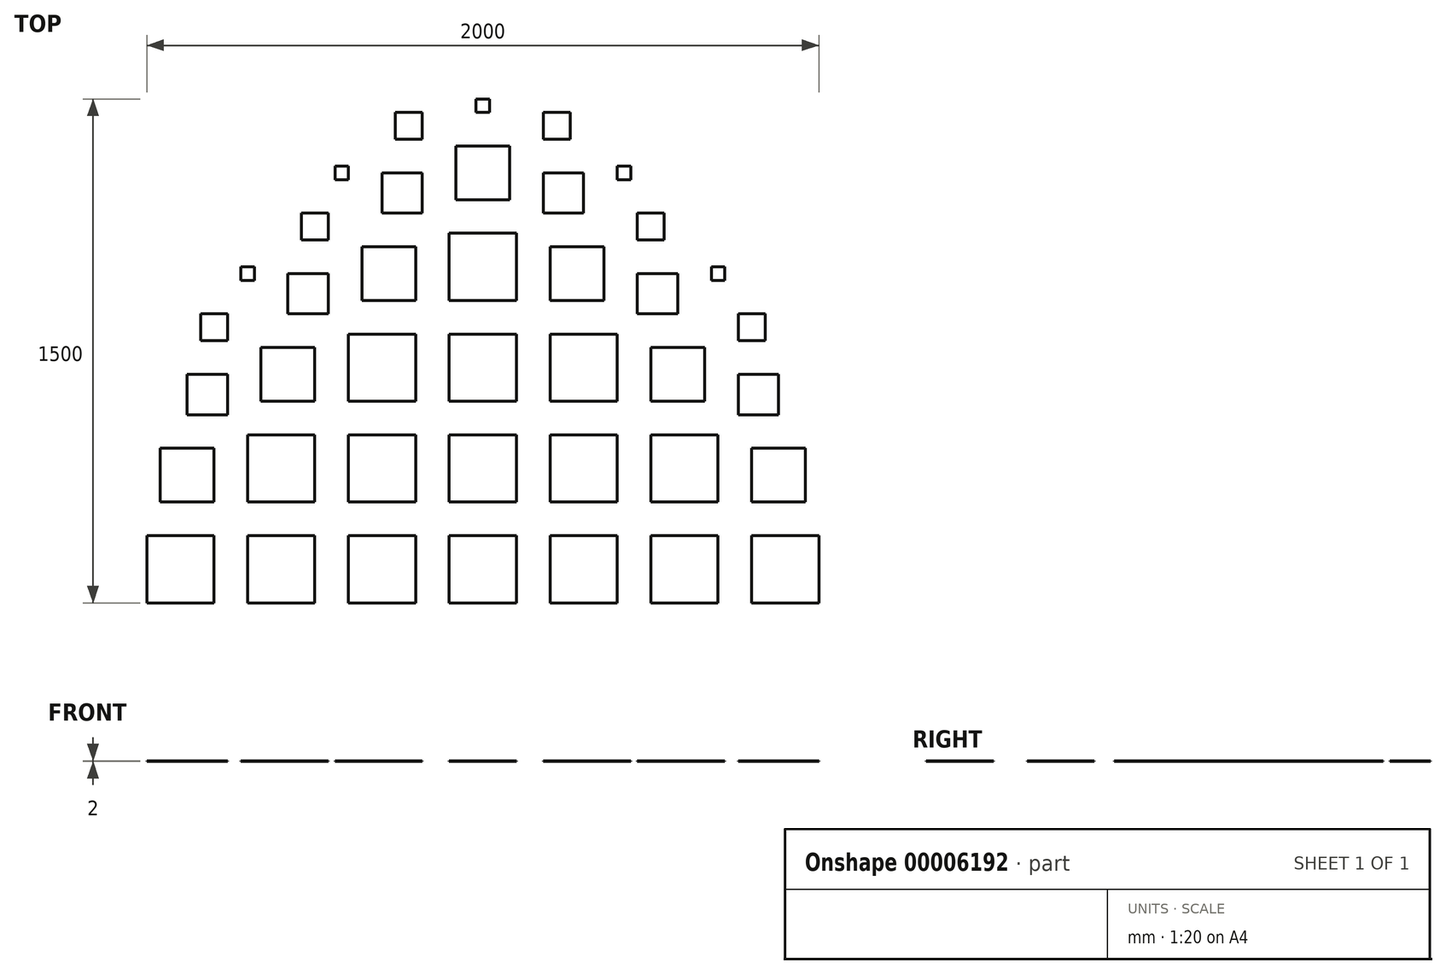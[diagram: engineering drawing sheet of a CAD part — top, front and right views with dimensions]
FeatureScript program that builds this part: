
annotation { "Feature Type Name" : "Feature", "Feature Type Description" : "" }
export const myFeature = defineFeature(function(context is Context, id is Id, definition is map)
    precondition{}
    {
        {
            var Q0;
            Q0=qCreatedBy(makeId("Top.planeOp"),FACE);
            var sketch = newSketch(context, id + "F0", { "sketchPlane" : qUnion([Q0])});
            skLineSegment(sketch, "E0.rect.bottom", {"start": v(100, 100) * mm, "end": v(-100, 100) * mm});
            skLineSegment(sketch, "E0.rect.top", {"start": v(100, -100) * mm, "end": v(-100, -100) * mm});
            skLineSegment(sketch, "E0.rect.left", {"start": v(100, 100) * mm, "end": v(100, -100) * mm});
            skLineSegment(sketch, "E0.rect.right", {"start": v(-100, 100) * mm, "end": v(-100, -100) * mm});
            skPoint(sketch, "E0.rect.middle", {"position": v(0, 0) * mm});
            skLineSegment(sketch, "E1.0.1.1", {"start": v(100, 200) * mm, "end": v(-60, 200) * mm});
            skLineSegment(sketch, "E1.0.1.3", {"start": v(100, 360) * mm, "end": v(100, 200) * mm});
            skLineSegment(sketch, "E1.1.0.0", {"start": v(200, 100) * mm, "end": v(200, -100) * mm});
            skLineSegment(sketch, "E1.1.0.1", {"start": v(400, -100) * mm, "end": v(200, -100) * mm});
            skLineSegment(sketch, "E1.1.0.2", {"start": v(400, 100) * mm, "end": v(200, 100) * mm});
            skLineSegment(sketch, "E1.1.0.3", {"start": v(400, 100) * mm, "end": v(400, -100) * mm});
            skLineSegment(sketch, "E1.1.1.0", {"start": v(200, 400) * mm, "end": v(200, 200) * mm});
            skLineSegment(sketch, "E1.1.1.1", {"start": v(400, 200) * mm, "end": v(200, 200) * mm});
            skLineSegment(sketch, "E1.1.1.2", {"start": v(400, 400) * mm, "end": v(200, 400) * mm});
            skLineSegment(sketch, "E1.1.1.3", {"start": v(400, 400) * mm, "end": v(400, 200) * mm});
            skLineSegment(sketch, "E1.2.0.0", {"start": v(500, 100) * mm, "end": v(500, -100) * mm});
            skLineSegment(sketch, "E1.2.0.1", {"start": v(700, -100) * mm, "end": v(500, -100) * mm});
            skLineSegment(sketch, "E1.2.0.2", {"start": v(700, 100) * mm, "end": v(500, 100) * mm});
            skLineSegment(sketch, "E1.2.0.3", {"start": v(700, 100) * mm, "end": v(700, -100) * mm});
            skLineSegment(sketch, "E1.2.1.0", {"start": v(500, 400) * mm, "end": v(500, 200) * mm});
            skLineSegment(sketch, "E1.2.1.1", {"start": v(700, 200) * mm, "end": v(500, 200) * mm});
            skLineSegment(sketch, "E1.2.1.2", {"start": v(700, 400) * mm, "end": v(500, 400) * mm});
            skLineSegment(sketch, "E1.2.1.3", {"start": v(700, 400) * mm, "end": v(700, 200) * mm});
            skLineSegment(sketch, "E1.3.0.0", {"start": v(800, 100) * mm, "end": v(800, -100) * mm});
            skLineSegment(sketch, "E1.3.0.1", {"start": v(1000, -100) * mm, "end": v(800, -100) * mm});
            skLineSegment(sketch, "E1.3.0.2", {"start": v(1000, 100) * mm, "end": v(800, 100) * mm});
            skLineSegment(sketch, "E1.3.0.3", {"start": v(1000, 100) * mm, "end": v(1000, -100) * mm});
            skLineSegment(sketch, "E1.3.1.0", {"start": v(800, 400) * mm, "end": v(800, 200) * mm});
            skLineSegment(sketch, "E1.3.1.1", {"start": v(1000, 200) * mm, "end": v(800, 200) * mm});
            skLineSegment(sketch, "E1.3.1.2", {"start": v(1000, 400) * mm, "end": v(800, 400) * mm});
            skLineSegment(sketch, "E1.3.1.3", {"start": v(1000, 400) * mm, "end": v(1000, 200) * mm});
            skLineSegment(sketch, "E1.4.0.0", {"start": v(1100, 100) * mm, "end": v(1100, -100) * mm});
            skLineSegment(sketch, "E1.4.0.1", {"start": v(1300, -100) * mm, "end": v(1100, -100) * mm});
            skLineSegment(sketch, "E1.4.0.2", {"start": v(1300, 100) * mm, "end": v(1100, 100) * mm});
            skLineSegment(sketch, "E1.4.0.3", {"start": v(1300, 100) * mm, "end": v(1300, -100) * mm});
            skLineSegment(sketch, "E1.4.1.0", {"start": v(1100, 400) * mm, "end": v(1100, 200) * mm});
            skLineSegment(sketch, "E1.4.1.1", {"start": v(1300, 200) * mm, "end": v(1100, 200) * mm});
            skLineSegment(sketch, "E1.4.1.2", {"start": v(1300, 400) * mm, "end": v(1100, 400) * mm});
            skLineSegment(sketch, "E1.4.1.3", {"start": v(1300, 400) * mm, "end": v(1300, 200) * mm});
            skLineSegment(sketch, "E1.5.0.0", {"start": v(1400, 100) * mm, "end": v(1400, -100) * mm});
            skLineSegment(sketch, "E1.5.0.1", {"start": v(1600, -100) * mm, "end": v(1400, -100) * mm});
            skLineSegment(sketch, "E1.5.0.2", {"start": v(1600, 100) * mm, "end": v(1400, 100) * mm});
            skLineSegment(sketch, "E1.5.0.3", {"start": v(1600, 100) * mm, "end": v(1600, -100) * mm});
            skLineSegment(sketch, "E1.5.1.0", {"start": v(1400, 400) * mm, "end": v(1400, 200) * mm});
            skLineSegment(sketch, "E1.5.1.1", {"start": v(1600, 200) * mm, "end": v(1400, 200) * mm});
            skLineSegment(sketch, "E1.5.1.2", {"start": v(1600, 400) * mm, "end": v(1400, 400) * mm});
            skLineSegment(sketch, "E1.5.1.3", {"start": v(1600, 400) * mm, "end": v(1600, 200) * mm});
            skLineSegment(sketch, "E1.6.0.0", {"start": v(1700, 100) * mm, "end": v(1700, -100) * mm});
            skLineSegment(sketch, "E1.6.0.1", {"start": v(1900, -100) * mm, "end": v(1700, -100) * mm});
            skLineSegment(sketch, "E1.6.0.2", {"start": v(1900, 100) * mm, "end": v(1700, 100) * mm});
            skLineSegment(sketch, "E1.6.0.3", {"start": v(1900, 100) * mm, "end": v(1900, -100) * mm});
            skLineSegment(sketch, "E1.6.1.0", {"start": v(1700, 360) * mm, "end": v(1700, 200) * mm});
            skLineSegment(sketch, "E1.6.1.1", {"start": v(1860, 200) * mm, "end": v(1700, 200) * mm});
            skLineSegment(sketch, "E1.direction1", {"start": v(-100, 100) * mm, "end": v(200, 100) * mm, "construction": true});
            skLineSegment(sketch, "E1.direction2", {"start": v(-100, 100) * mm, "end": v(-100, 200) * mm, "construction": true});
            skLineSegment(sketch, "E2", {"start": v(-60, 200) * mm, "end": v(-60, 360) * mm});
            skLineSegment(sketch, "E3", {"start": v(-60, 360) * mm, "end": v(100, 360) * mm});
            skPoint(sketch, "E4.orphan", {"position": v(100, 400) * mm});
            skLineSegment(sketch, "E5", {"start": v(1860, 200) * mm, "end": v(1860, 360) * mm});
            skLineSegment(sketch, "E6", {"start": v(1860, 360) * mm, "end": v(1700, 360) * mm});
            skPoint(sketch, "E7.orphan", {"position": v(1700, 400) * mm});
            skPoint(sketch, "E8.orphan", {"position": v(1900, 200) * mm});
            skLineSegment(sketch, "E9.0.1.0", {"start": v(700, 700) * mm, "end": v(500, 700) * mm});
            skLineSegment(sketch, "E9.0.1.1", {"start": v(500, 700) * mm, "end": v(500, 500) * mm});
            skLineSegment(sketch, "E9.0.1.2", {"start": v(700, 700) * mm, "end": v(700, 500) * mm});
            skLineSegment(sketch, "E9.0.1.3", {"start": v(700, 500) * mm, "end": v(500, 500) * mm});
            skLineSegment(sketch, "E9.direction1", {"start": v(500, 200) * mm, "end": v(550, 200) * mm, "construction": true});
            skLineSegment(sketch, "E9.direction2", {"start": v(500, 200) * mm, "end": v(500, 500) * mm, "construction": true});
            skLineSegment(sketch, "E10.1.0.0", {"start": v(1000, 700) * mm, "end": v(1000, 500) * mm});
            skLineSegment(sketch, "E10.1.0.1", {"start": v(1000, 700) * mm, "end": v(800, 700) * mm});
            skLineSegment(sketch, "E10.1.0.2", {"start": v(1000, 500) * mm, "end": v(800, 500) * mm});
            skLineSegment(sketch, "E10.1.0.3", {"start": v(800, 700) * mm, "end": v(800, 500) * mm});
            skLineSegment(sketch, "E10.2.0.0", {"start": v(1300, 700) * mm, "end": v(1300, 500) * mm});
            skLineSegment(sketch, "E10.2.0.1", {"start": v(1300, 700) * mm, "end": v(1100, 700) * mm});
            skLineSegment(sketch, "E10.2.0.2", {"start": v(1300, 500) * mm, "end": v(1100, 500) * mm});
            skLineSegment(sketch, "E10.2.0.3", {"start": v(1100, 700) * mm, "end": v(1100, 500) * mm});
            skLineSegment(sketch, "E10.direction1", {"start": v(500, 700) * mm, "end": v(800, 700) * mm, "construction": true});
            skLineSegment(sketch, "E11.0.1.0", {"start": v(1000, 800) * mm, "end": v(800, 800) * mm});
            skLineSegment(sketch, "E11.0.1.1", {"start": v(1000, 1000) * mm, "end": v(1000, 800) * mm});
            skLineSegment(sketch, "E11.0.1.2", {"start": v(800, 1000) * mm, "end": v(800, 800) * mm});
            skLineSegment(sketch, "E11.0.1.3", {"start": v(1000, 1000) * mm, "end": v(800, 1000) * mm});
            skLineSegment(sketch, "E11.direction1", {"start": v(800, 700) * mm, "end": v(850, 700) * mm, "construction": true});
            skLineSegment(sketch, "E11.direction2", {"start": v(800, 700) * mm, "end": v(800, 1000) * mm, "construction": true});
            skLineSegment(sketch, "E12.bottom", {"start": v(400, 500) * mm, "end": v(240, 500) * mm});
            skLineSegment(sketch, "E12.top", {"start": v(400, 660) * mm, "end": v(240, 660) * mm});
            skLineSegment(sketch, "E12.left", {"start": v(400, 500) * mm, "end": v(400, 660) * mm});
            skLineSegment(sketch, "E12.right", {"start": v(240, 500) * mm, "end": v(240, 660) * mm});
            skLineSegment(sketch, "E13.bottom", {"start": v(1400, 500) * mm, "end": v(1560, 500) * mm});
            skLineSegment(sketch, "E13.top", {"start": v(1400, 660) * mm, "end": v(1560, 660) * mm});
            skLineSegment(sketch, "E13.left", {"start": v(1400, 500) * mm, "end": v(1400, 660) * mm});
            skLineSegment(sketch, "E13.right", {"start": v(1560, 500) * mm, "end": v(1560, 660) * mm});
            skLineSegment(sketch, "E14.bottom", {"start": v(700, 800) * mm, "end": v(540, 800) * mm});
            skLineSegment(sketch, "E14.top", {"start": v(700, 960) * mm, "end": v(540, 960) * mm});
            skLineSegment(sketch, "E14.left", {"start": v(700, 800) * mm, "end": v(700, 960) * mm});
            skLineSegment(sketch, "E14.right", {"start": v(540, 800) * mm, "end": v(540, 960) * mm});
            skLineSegment(sketch, "E15.bottom", {"start": v(1100, 800) * mm, "end": v(1260, 800) * mm});
            skLineSegment(sketch, "E15.top", {"start": v(1100, 960) * mm, "end": v(1260, 960) * mm});
            skLineSegment(sketch, "E15.left", {"start": v(1100, 800) * mm, "end": v(1100, 960) * mm});
            skLineSegment(sketch, "E15.right", {"start": v(1260, 800) * mm, "end": v(1260, 960) * mm});
            skLineSegment(sketch, "E16.bottom", {"start": v(20, 460) * mm, "end": v(140, 460) * mm});
            skLineSegment(sketch, "E16.top", {"start": v(20, 580) * mm, "end": v(140, 580) * mm});
            skLineSegment(sketch, "E16.left", {"start": v(20, 460) * mm, "end": v(20, 580) * mm});
            skLineSegment(sketch, "E16.right", {"start": v(140, 460) * mm, "end": v(140, 580) * mm});
            skLineSegment(sketch, "E17.bottom", {"start": v(1660, 460) * mm, "end": v(1780, 460) * mm});
            skLineSegment(sketch, "E17.top", {"start": v(1660, 580) * mm, "end": v(1780, 580) * mm});
            skLineSegment(sketch, "E17.left", {"start": v(1660, 460) * mm, "end": v(1660, 580) * mm});
            skLineSegment(sketch, "E17.right", {"start": v(1780, 460) * mm, "end": v(1780, 580) * mm});
            skLineSegment(sketch, "E18.bottom", {"start": v(1360, 760) * mm, "end": v(1480, 760) * mm});
            skLineSegment(sketch, "E18.top", {"start": v(1360, 880) * mm, "end": v(1480, 880) * mm});
            skLineSegment(sketch, "E18.left", {"start": v(1360, 760) * mm, "end": v(1360, 880) * mm});
            skLineSegment(sketch, "E18.right", {"start": v(1480, 760) * mm, "end": v(1480, 880) * mm});
            skLineSegment(sketch, "E19.bottom", {"start": v(440, 760) * mm, "end": v(320, 760) * mm});
            skLineSegment(sketch, "E19.top", {"start": v(440, 880) * mm, "end": v(320, 880) * mm});
            skLineSegment(sketch, "E19.left", {"start": v(440, 760) * mm, "end": v(440, 880) * mm});
            skLineSegment(sketch, "E19.right", {"start": v(320, 760) * mm, "end": v(320, 880) * mm});
            skLineSegment(sketch, "E20.rect.bottom", {"start": v(820, 1260) * mm, "end": v(980, 1260) * mm});
            skLineSegment(sketch, "E20.rect.top", {"start": v(820, 1100) * mm, "end": v(980, 1100) * mm});
            skLineSegment(sketch, "E20.rect.left", {"start": v(820, 1260) * mm, "end": v(820, 1100) * mm});
            skLineSegment(sketch, "E20.rect.right", {"start": v(980, 1260) * mm, "end": v(980, 1100) * mm});
            skPoint(sketch, "E20.rect.middle", {"position": v(900, 1180) * mm});
            skLineSegment(sketch, "E21.bottom", {"start": v(720, 1060) * mm, "end": v(600, 1060) * mm});
            skLineSegment(sketch, "E21.top", {"start": v(720, 1180) * mm, "end": v(600, 1180) * mm});
            skLineSegment(sketch, "E21.left", {"start": v(720, 1060) * mm, "end": v(720, 1180) * mm});
            skLineSegment(sketch, "E21.right", {"start": v(600, 1060) * mm, "end": v(600, 1180) * mm});
            skLineSegment(sketch, "E22.bottom", {"start": v(1080, 1060) * mm, "end": v(1200, 1060) * mm});
            skLineSegment(sketch, "E22.top", {"start": v(1080, 1180) * mm, "end": v(1200, 1180) * mm});
            skLineSegment(sketch, "E22.left", {"start": v(1080, 1060) * mm, "end": v(1080, 1180) * mm});
            skLineSegment(sketch, "E22.right", {"start": v(1200, 1060) * mm, "end": v(1200, 1180) * mm});
            skLineSegment(sketch, "E23.bottom", {"start": v(60, 680) * mm, "end": v(140, 680) * mm});
            skLineSegment(sketch, "E23.top", {"start": v(60, 760) * mm, "end": v(140, 760) * mm});
            skLineSegment(sketch, "E23.left", {"start": v(60, 680) * mm, "end": v(60, 760) * mm});
            skLineSegment(sketch, "E23.right", {"start": v(140, 680) * mm, "end": v(140, 760) * mm});
            skLineSegment(sketch, "E24.bottom", {"start": v(360, 980) * mm, "end": v(440, 980) * mm});
            skLineSegment(sketch, "E24.top", {"start": v(360, 1060) * mm, "end": v(440, 1060) * mm});
            skLineSegment(sketch, "E24.left", {"start": v(360, 980) * mm, "end": v(360, 1060) * mm});
            skLineSegment(sketch, "E24.right", {"start": v(440, 980) * mm, "end": v(440, 1060) * mm});
            skLineSegment(sketch, "E25.bottom", {"start": v(640, 1280) * mm, "end": v(720, 1280) * mm});
            skLineSegment(sketch, "E25.top", {"start": v(640, 1360) * mm, "end": v(720, 1360) * mm});
            skLineSegment(sketch, "E25.left", {"start": v(640, 1280) * mm, "end": v(640, 1360) * mm});
            skLineSegment(sketch, "E25.right", {"start": v(720, 1280) * mm, "end": v(720, 1360) * mm});
            skLineSegment(sketch, "E26.bottom", {"start": v(180, 860) * mm, "end": v(220, 860) * mm});
            skLineSegment(sketch, "E26.top", {"start": v(180, 900) * mm, "end": v(220, 900) * mm});
            skLineSegment(sketch, "E26.left", {"start": v(180, 860) * mm, "end": v(180, 900) * mm});
            skLineSegment(sketch, "E26.right", {"start": v(220, 860) * mm, "end": v(220, 900) * mm});
            skLineSegment(sketch, "E27.bottom", {"start": v(460, 1160) * mm, "end": v(500, 1160) * mm});
            skLineSegment(sketch, "E27.top", {"start": v(460, 1200) * mm, "end": v(500, 1200) * mm});
            skLineSegment(sketch, "E27.left", {"start": v(460, 1160) * mm, "end": v(460, 1200) * mm});
            skLineSegment(sketch, "E27.right", {"start": v(500, 1160) * mm, "end": v(500, 1200) * mm});
            skLineSegment(sketch, "E28", {"start": v(900, 1180) * mm, "end": v(900, 1613.01) * mm, "construction": true});
            skLineSegment(sketch, "E29.0.MirrorCS", {"start": v(1160, 1280) * mm, "end": v(1160, 1360) * mm});
            skLineSegment(sketch, "E30.0.MirrorCS", {"start": v(1160, 1280) * mm, "end": v(1080, 1280) * mm});
            skLineSegment(sketch, "E31.0.MirrorCS", {"start": v(1160, 1360) * mm, "end": v(1080, 1360) * mm});
            skLineSegment(sketch, "E32.0.MirrorCS", {"start": v(1080, 1280) * mm, "end": v(1080, 1360) * mm});
            skLineSegment(sketch, "E33.0.MirrorCS", {"start": v(1340, 1200) * mm, "end": v(1300, 1200) * mm});
            skLineSegment(sketch, "E34.0.MirrorCS", {"start": v(1340, 1160) * mm, "end": v(1340, 1200) * mm});
            skLineSegment(sketch, "E35.0.MirrorCS", {"start": v(1340, 1160) * mm, "end": v(1300, 1160) * mm});
            skLineSegment(sketch, "E36.0.MirrorCS", {"start": v(1300, 1160) * mm, "end": v(1300, 1200) * mm});
            skLineSegment(sketch, "E37.0.MirrorCS", {"start": v(1440, 980) * mm, "end": v(1440, 1060) * mm});
            skLineSegment(sketch, "E38.0.MirrorCS", {"start": v(1440, 980) * mm, "end": v(1360, 980) * mm});
            skLineSegment(sketch, "E39.0.MirrorCS", {"start": v(1360, 980) * mm, "end": v(1360, 1060) * mm});
            skLineSegment(sketch, "E40.0.MirrorCS", {"start": v(1440, 1060) * mm, "end": v(1360, 1060) * mm});
            skLineSegment(sketch, "E41.0.MirrorCS", {"start": v(1620, 900) * mm, "end": v(1580, 900) * mm});
            skLineSegment(sketch, "E42.0.MirrorCS", {"start": v(1620, 860) * mm, "end": v(1620, 900) * mm});
            skLineSegment(sketch, "E43.0.MirrorCS", {"start": v(1620, 860) * mm, "end": v(1580, 860) * mm});
            skLineSegment(sketch, "E44.0.MirrorCS", {"start": v(1580, 860) * mm, "end": v(1580, 900) * mm});
            skLineSegment(sketch, "E45.0.MirrorCS", {"start": v(1740, 760) * mm, "end": v(1660, 760) * mm});
            skLineSegment(sketch, "E46.0.MirrorCS", {"start": v(1740, 680) * mm, "end": v(1740, 760) * mm});
            skLineSegment(sketch, "E47.0.MirrorCS", {"start": v(1740, 680) * mm, "end": v(1660, 680) * mm});
            skLineSegment(sketch, "E48.rect.bottom", {"start": v(920, 1400) * mm, "end": v(880, 1400) * mm});
            skLineSegment(sketch, "E48.rect.top", {"start": v(920, 1360) * mm, "end": v(880, 1360) * mm});
            skLineSegment(sketch, "E48.rect.left", {"start": v(920, 1400) * mm, "end": v(920, 1360) * mm});
            skLineSegment(sketch, "E48.rect.right", {"start": v(880, 1400) * mm, "end": v(880, 1360) * mm});
            skPoint(sketch, "E48.rect.middle", {"position": v(900, 1380) * mm});
            skLineSegment(sketch, "E49", {"start": v(1660, 760) * mm, "end": v(1660, 680) * mm});
            skSolve(sketch);
        }
        {
            var Q0;
            Q0 = qSketchRegion(id + "F0", true);
            extrude(context, id + "F1", {"entities" : qUnion([Q0]), "oppositeDirection" : true, "depth" : 2 * mm});
        }
    });
